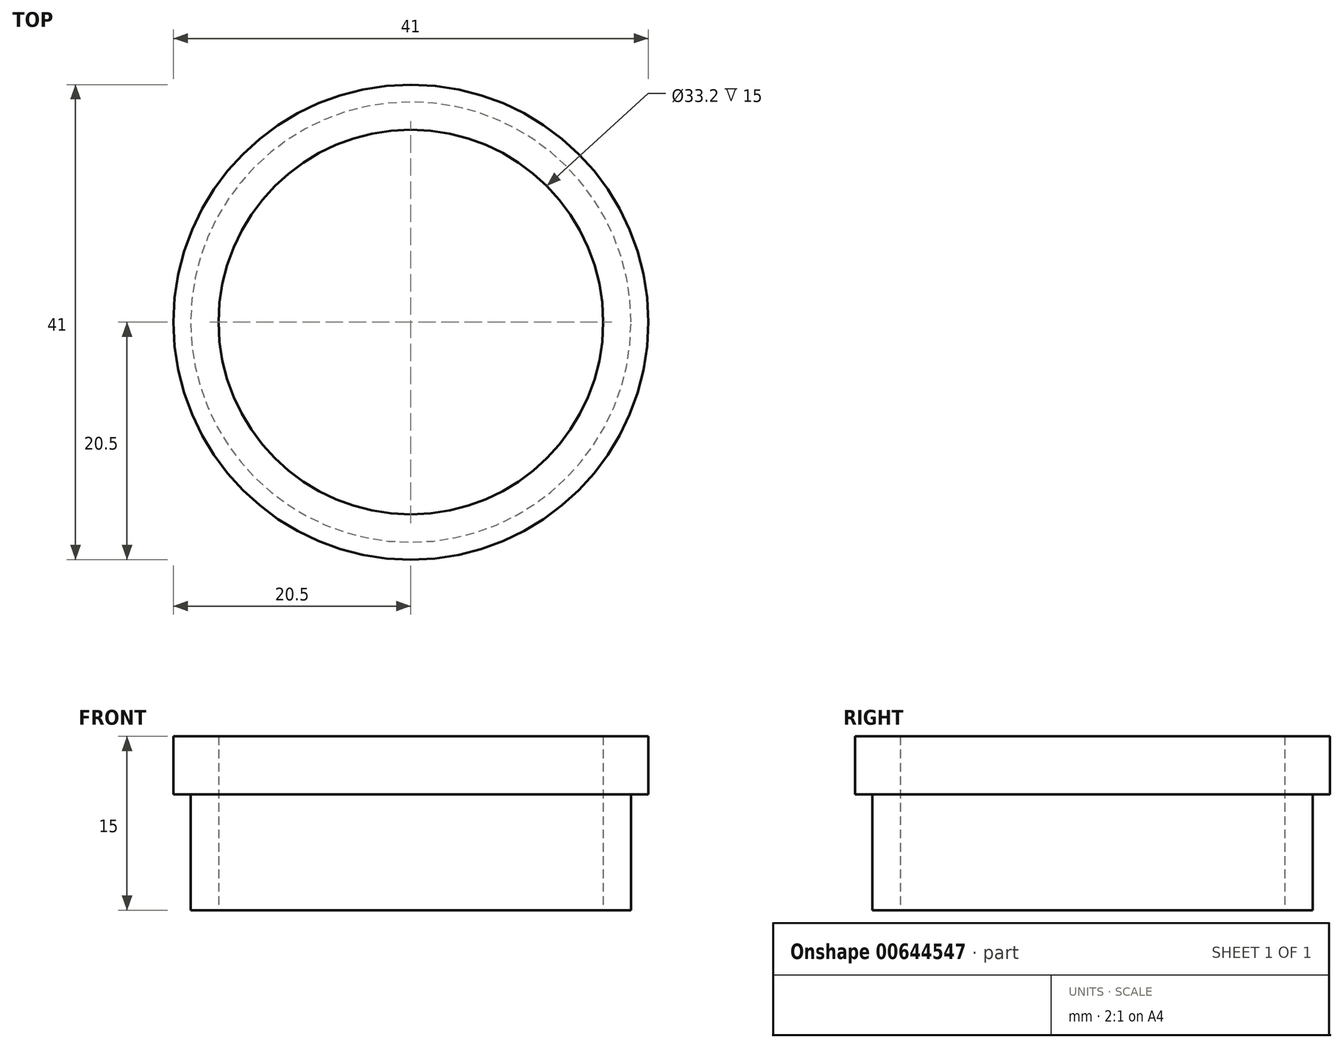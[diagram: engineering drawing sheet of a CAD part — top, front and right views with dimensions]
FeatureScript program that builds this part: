
annotation { "Feature Type Name" : "Feature", "Feature Type Description" : "" }
export const myFeature = defineFeature(function(context is Context, id is Id, definition is map)
    precondition{}
    {
        {
            var Q0;
            Q0=qCreatedBy(makeId("Top.planeOp"),FACE);
            var sketch = newSketch(context, id + "F0", { "sketchPlane" : qUnion([Q0])});
            skCircle(sketch, "E0", {"center": v(0, 0) * mm, "radius": 19 * mm});
            skSolve(sketch);
        }
        {
            var Q0;
            Q0 = qSketchRegion(id + "F0", true);
            extrude(context, id + "F1", {"entities" : qUnion([Q0]), "depth" : 10 * mm, "offsetDistance" : 25 * mm});
        }
        {
            var Q0;
            Q0=makeQuery(id+"F1.opExtrude","CAP_FACE",FACE,{"disambiguationData":[OSD([sQuery(id+"F0.wireOp",EDGE,"E0")])],"isStart":false});
            var sketch = newSketch(context, id + "F2", { "sketchPlane" : qUnion([Q0])});
            skCircle(sketch, "E1", {"center": v(0, 0) * mm, "radius": 20.5 * mm});
            skSolve(sketch);
        }
        {
            var Q0;
            Q0 = qSketchRegion(id + "F2", true);
            extrude(context, id + "F3", {"entities" : qUnion([Q0]), "operationType" : NewBodyOperationType.ADD, "depth" : 5 * mm, "offsetDistance" : 25 * mm});
        }
        {
            var Q0;
            Q0=makeQuery(id+"F1.opExtrude","CAP_FACE",FACE,{"disambiguationData":[OSD([sQuery(id+"F0.wireOp",EDGE,"E0")])],"isStart":true});
            var sketch = newSketch(context, id + "F4", { "sketchPlane" : qUnion([Q0])});
            skCircle(sketch, "E2", {"center": v(0, 0) * mm, "radius": 16.6 * mm});
            skSolve(sketch);
        }
        {
            var Q0;
            Q0 = qSketchRegion(id + "F4", true);
            extrude(context, id + "F5", {"entities" : qUnion([Q0]), "operationType" : NewBodyOperationType.REMOVE, "endBound" : BoundingType.THROUGH_ALL, "oppositeDirection" : true, "depth" : 25 * mm, "offsetDistance" : 25 * mm});
        }
    });
